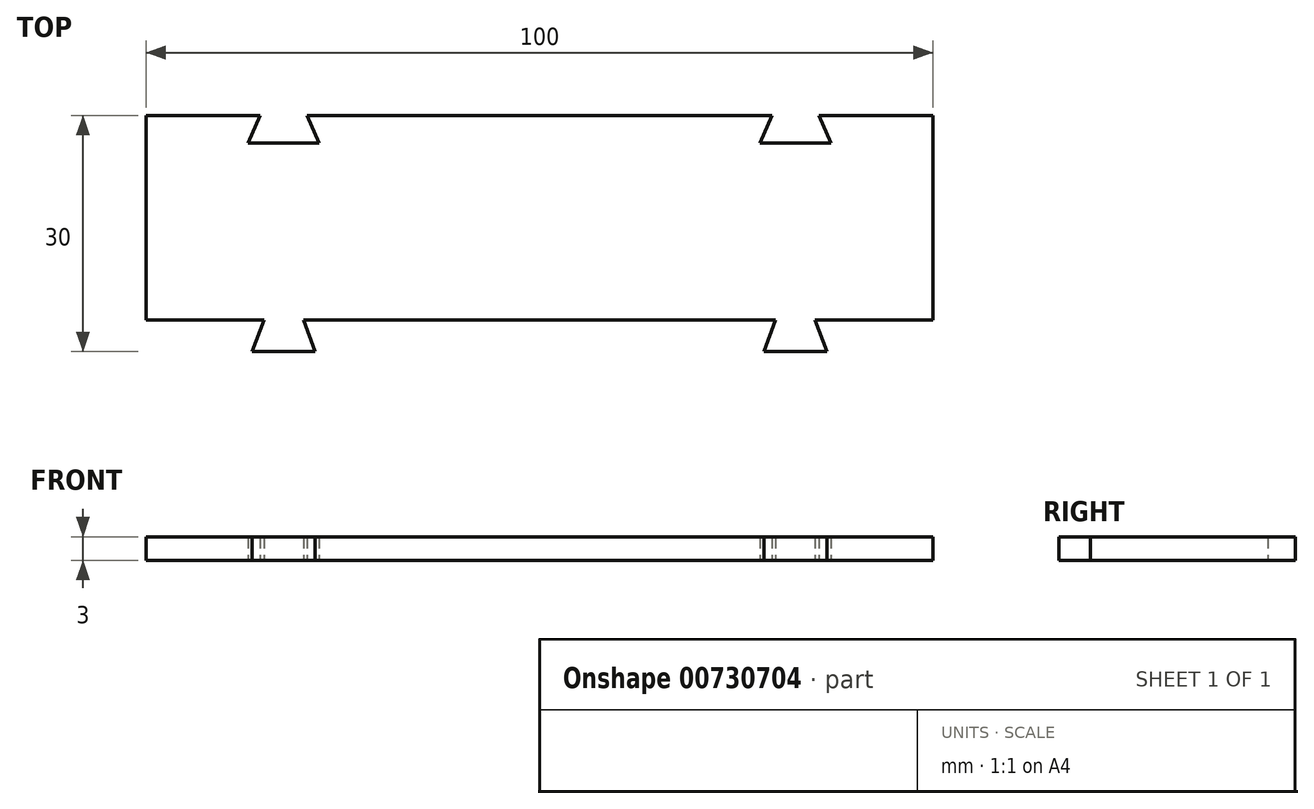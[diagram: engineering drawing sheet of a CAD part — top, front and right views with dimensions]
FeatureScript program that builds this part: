
annotation { "Feature Type Name" : "Feature", "Feature Type Description" : "" }
export const myFeature = defineFeature(function(context is Context, id is Id, definition is map)
    precondition{}
    {
        {
            var Q0;
            Q0=qCreatedBy(makeId("Top.planeOp"),FACE);
            var sketch = newSketch(context, id + "F0", { "sketchPlane" : qUnion([Q0])});
            skLineSegment(sketch, "E0.bottom", {"start": v(50, -13) * mm, "end": v(-50, -13) * mm});
            skLineSegment(sketch, "E0.top", {"start": v(50, 13) * mm, "end": v(-50, 13) * mm});
            skLineSegment(sketch, "E0.left", {"start": v(50, -13) * mm, "end": v(50, 13) * mm});
            skLineSegment(sketch, "E0.right", {"start": v(-50, -13) * mm, "end": v(-50, 13) * mm});
            skPoint(sketch, "E0.middle", {"position": v(0, 0) * mm});
            skLineSegment(sketch, "E1", {"start": v(-50, -13) * mm, "end": v(-35, -13) * mm, "construction": true});
            skLineSegment(sketch, "E2", {"start": v(50, -13) * mm, "end": v(35, -13) * mm, "construction": true});
            skLineSegment(sketch, "E3", {"start": v(-50, 13) * mm, "end": v(-35.5, 13) * mm, "construction": true});
            skLineSegment(sketch, "E4", {"start": v(50, 13) * mm, "end": v(35.5, 13) * mm, "construction": true});
            skLineSegment(sketch, "E5", {"start": v(-35, -13) * mm, "end": v(-30, -13) * mm, "construction": true});
            skLineSegment(sketch, "E6", {"start": v(-35, -13) * mm, "end": v(-36.5, -17) * mm});
            skLineSegment(sketch, "E7", {"start": v(-36.5, -17) * mm, "end": v(-28.5, -17) * mm});
            skLineSegment(sketch, "E8", {"start": v(-28.5, -17) * mm, "end": v(-30, -13) * mm});
            skLineSegment(sketch, "E9", {"start": v(-32.5, -17) * mm, "end": v(-32.5, -13) * mm, "construction": true});
            skLineSegment(sketch, "E10", {"start": v(-35.5, 13) * mm, "end": v(-29.5, 13) * mm, "construction": true});
            skLineSegment(sketch, "E11", {"start": v(-35.5, 13) * mm, "end": v(-37, 9.5) * mm});
            skLineSegment(sketch, "E12", {"start": v(-37, 9.5) * mm, "end": v(-28, 9.5) * mm});
            skLineSegment(sketch, "E13", {"start": v(-28, 9.5) * mm, "end": v(-29.5, 13) * mm});
            skPoint(sketch, "E14.endSnap0", {"position": v(-32.5, 9.5) * mm});
            skLineSegment(sketch, "E15", {"start": v(-32.5, 9.5) * mm, "end": v(-32.5, 13) * mm, "construction": true});
            skLineSegment(sketch, "E16", {"start": v(35.5, 13) * mm, "end": v(29.5, 13) * mm, "construction": true});
            skLineSegment(sketch, "E17", {"start": v(35, -13) * mm, "end": v(30, -13) * mm, "construction": true});
            skLineSegment(sketch, "E18", {"start": v(35.5, 13) * mm, "end": v(37, 9.5) * mm});
            skLineSegment(sketch, "E19", {"start": v(37, 9.5) * mm, "end": v(28, 9.5) * mm});
            skLineSegment(sketch, "E20", {"start": v(28, 9.5) * mm, "end": v(29.5, 13) * mm});
            skLineSegment(sketch, "E21", {"start": v(35, -13) * mm, "end": v(36.5, -17) * mm});
            skLineSegment(sketch, "E22", {"start": v(36.5, -17) * mm, "end": v(28.5, -17) * mm});
            skLineSegment(sketch, "E23", {"start": v(28.5, -17) * mm, "end": v(30, -13) * mm});
            skLineSegment(sketch, "E24", {"start": v(32.5, 9.5) * mm, "end": v(32.5, 13) * mm, "construction": true});
            skLineSegment(sketch, "E25", {"start": v(32.5, -17) * mm, "end": v(32.5, -13) * mm, "construction": true});
            skSolve(sketch);
        }
        {
            var Q0;
            {var subQ0=sQuery(id+"F0.wireOp",EDGE,"E0.left");Q0=makeQuery(id+"F0.imprint","IMPRINT",FACE,{"disambiguationData":[TD([[makeQuery(id+"F0.imprint","IMPRINT",EDGE,{"derivedFrom":subQ0}),1.0]])]});}
            var Q1;
            {var subQ0=sQuery(id+"F0.wireOp",EDGE,"E6");Q1=makeQuery(id+"F0.imprint","IMPRINT",FACE,{"disambiguationData":[TD([[makeQuery(id+"F0.imprint","IMPRINT",EDGE,{"derivedFrom":subQ0}),1.0]])]});}
            var Q2;
            {var subQ0=sQuery(id+"F0.wireOp",EDGE,"E21");Q2=makeQuery(id+"F0.imprint","IMPRINT",FACE,{"disambiguationData":[TD([[makeQuery(id+"F0.imprint","IMPRINT",EDGE,{"derivedFrom":subQ0}),-1.0]])]});}
            extrude(context, id + "F1", {"entities" : qUnion([Q0, Q1, Q2]), "depth" : 3 * mm, "offsetDistance" : 25 * mm});
        }
    });
